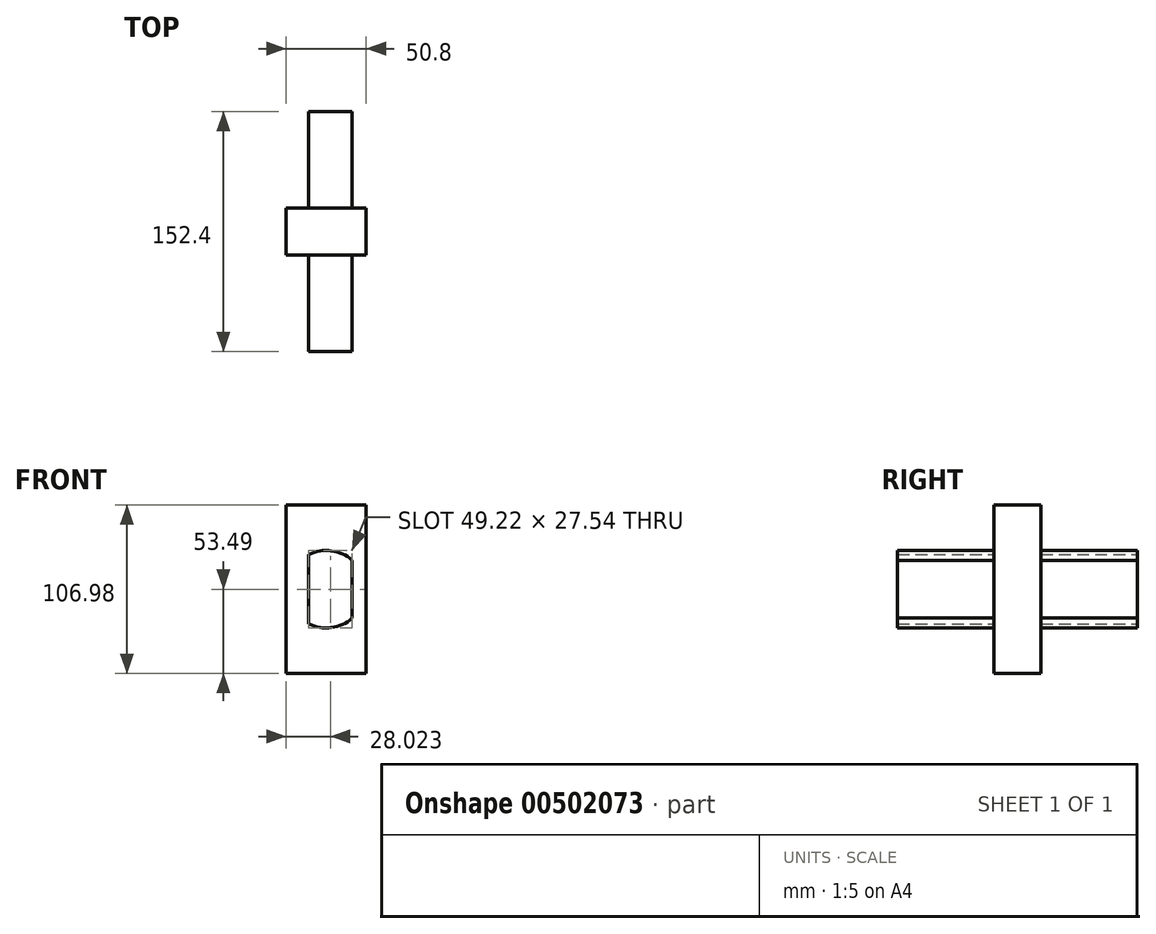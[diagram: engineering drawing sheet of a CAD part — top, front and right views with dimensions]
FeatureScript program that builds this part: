
annotation { "Feature Type Name" : "Feature", "Feature Type Description" : "" }
export const myFeature = defineFeature(function(context is Context, id is Id, definition is map)
    precondition{}
    {
        {
            var Q0;
            Q0=qCreatedBy(makeId("Front.planeOp"),FACE);
            var sketch = newSketch(context, id + "F0", { "sketchPlane" : qUnion([Q0])});
            skCircle(sketch, "E0", {"center": v(0, 0) * mm, "radius": 24.62 * mm});
            skLineSegment(sketch, "E1.bottom", {"start": v(16.4, -42.3) * mm, "end": v(-11.15, -42.3) * mm});
            skLineSegment(sketch, "E1.top", {"start": v(16.4, 42.3) * mm, "end": v(-11.15, 42.3) * mm});
            skLineSegment(sketch, "E1.left", {"start": v(16.4, -42.3) * mm, "end": v(16.4, 42.3) * mm});
            skLineSegment(sketch, "E1.right", {"start": v(-11.15, -42.3) * mm, "end": v(-11.15, 42.3) * mm});
            skPoint(sketch, "E1.middle", {"position": v(2.62, 0) * mm});
            skSolve(sketch);
        }
        {
            var Q0;
            {var subQ0=sQuery(id+"F0.wireOp",EDGE,"E1.right");var subQ1=sQuery(id+"F0.wireOp",EDGE,"E0");var subQ2=makeQuery(id+"F0.imprint","INTERSECT",VERTEX,{"disambiguationData":[OD(0.0)],"derivedFrom":[subQ1,subQ0]});Q0=makeQuery(id+"F0.imprint","IMPRINT",FACE,{"disambiguationData":[TD([[makeQuery(id+"F0.imprint","IMPRINT",EDGE,{"disambiguationData":[TD([[subQ2,-1.0]])],"derivedFrom":subQ1}),1.0]])]});}
            var Q1;
            {var subQ0=sQuery(id+"F0.wireOp",EDGE,"E1.left");var subQ1=sQuery(id+"F0.wireOp",EDGE,"E0");var subQ2=makeQuery(id+"F0.imprint","INTERSECT",VERTEX,{"disambiguationData":[OD(0.0)],"derivedFrom":[subQ1,subQ0]});Q1=makeQuery(id+"F0.imprint","IMPRINT",FACE,{"disambiguationData":[TD([[makeQuery(id+"F0.imprint","IMPRINT",EDGE,{"disambiguationData":[TD([[subQ2,1.0]])],"derivedFrom":subQ1}),1.0]])]});}
            extrude(context, id + "F1", {"entities" : qUnion([Q0, Q1]), "endBound" : BoundingType.SYMMETRIC, "depth" : 152.4 * mm});
        }
        {
            var Q0;
            Q0=qCreatedBy(makeId("Right.planeOp"),FACE);
            var sketch = newSketch(context, id + "F2", { "sketchPlane" : qUnion([Q0])});
            skLineSegment(sketch, "E2.bottom", {"start": v(-14.89, 53.49) * mm, "end": v(14.89, 53.49) * mm});
            skLineSegment(sketch, "E2.top", {"start": v(-14.89, -53.49) * mm, "end": v(14.89, -53.49) * mm});
            skLineSegment(sketch, "E2.left", {"start": v(-14.89, 53.49) * mm, "end": v(-14.89, -53.49) * mm});
            skLineSegment(sketch, "E2.right", {"start": v(14.89, 53.49) * mm, "end": v(14.89, -53.49) * mm});
            skPoint(sketch, "E2.middle", {"position": v(0, 0) * mm});
            skLineSegment(sketch, "E3", {"start": v(97.6, 0) * mm, "end": v(-96.22, 0) * mm, "construction": true});
            skSolve(sketch);
        }
        {
            var Q0;
            Q0 = qSketchRegion(id + "F2", true);
            extrude(context, id + "F3", {"entities" : qUnion([Q0]), "operationType" : NewBodyOperationType.ADD, "endBound" : BoundingType.SYMMETRIC, "depth" : 50.8 * mm});
        }
    });
